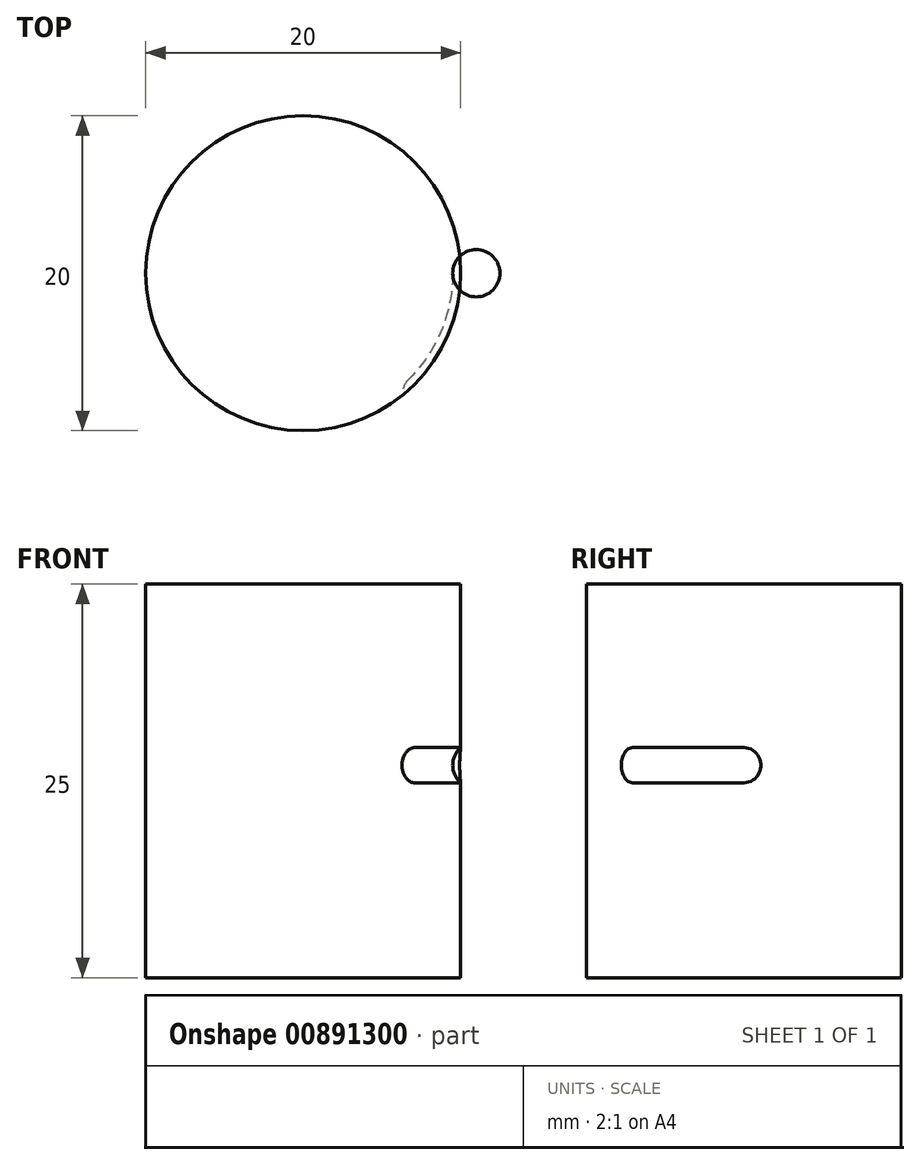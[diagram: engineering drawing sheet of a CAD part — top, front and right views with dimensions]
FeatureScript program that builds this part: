
annotation { "Feature Type Name" : "Feature", "Feature Type Description" : "" }
export const myFeature = defineFeature(function(context is Context, id is Id, definition is map)
    precondition{}
    {
        {
            var Q0;
            Q0=qCreatedBy(makeId("Top.planeOp"),FACE);
            var sketch = newSketch(context, id + "F0", { "sketchPlane" : qUnion([Q0])});
            skCircle(sketch, "E0", {"center": v(0, 0) * mm, "radius": 10 * mm});
            skSolve(sketch);
        }
        {
            var Q0;
            Q0 = qSketchRegion(id + "F0", true);
            extrude(context, id + "F1", {"entities" : qUnion([Q0]), "depth" : 25 * mm, "offsetDistance" : 25 * mm});
        }
        {
            var Q0;
            Q0=qCreatedBy(makeId("Front.planeOp"),FACE);
            var sketch = newSketch(context, id + "F2", { "sketchPlane" : qUnion([Q0])});
            skArc(sketch, "E1", {"start": v(11, 15) * mm, "mid": v(9.5, 13.5) * mm, "end": v(11, 12) * mm});
            skLineSegment(sketch, "E2", {"start": v(10, 25) * mm, "end": v(10, 0) * mm, "construction": true});
            skLineSegment(sketch, "E3", {"start": v(11, 15) * mm, "end": v(11, 12) * mm});
            skSolve(sketch);
        }
        {
            var Q0;
            Q0 = qSketchRegion(id + "F2", true);
            var Q1;
            Q1=makeQuery(id+"F1.opExtrude","CAP_EDGE",EDGE,{"disambiguationData":[OSD([sQuery(id+"F0.wireOp",EDGE,"E0")])],"isStart":false});
            revolve(context, id + "F3", {"operationType" : NewBodyOperationType.REMOVE, "surfaceOperationType" : NewSurfaceOperationType.NEW, "entities" : qUnion([Q0]), "axis" : qUnion([Q1]), "revolveType" : RevolveType.ONE_DIRECTION, "oppositeDirection" : true, "angle" : 45 * degree});
        }
        {
            var Q0;
            Q0=makeQuery(id+"F2.imprint","IMPRINT",FACE,{"disambiguationData":[TD([[makeQuery(id+"F2.imprint","IMPRINT",EDGE,{"derivedFrom":sQuery(id+"F2.wireOp",EDGE,"E1")}),1.0]])]});
            var Q1;
            Q1=sQuery(id+"F2.wireOp",EDGE,"E3");
            revolve(context, id + "F4", {"surfaceOperationType" : NewSurfaceOperationType.NEW, "entities" : qUnion([Q0]), "axis" : qUnion([Q1]), "revolveType" : RevolveType.FULL});
        }
        {
            var Q0;
            Q0=makeQuery(id+"F4.opRevolve","SWEPT_BODY",BODY,{"disambiguationData":[OSD([sQuery(id+"F2.wireOp",EDGE,"E1"),sQuery(id+"F2.wireOp",EDGE,"E3")])]});
            var Q1;
            Q1=makeQuery(id+"F1.opExtrude","CAP_EDGE",EDGE,{"disambiguationData":[OSD([sQuery(id+"F0.wireOp",EDGE,"E0")])],"isStart":false});
            transform(context, id + "F5", {"entities" : qUnion([Q0]), "transformType" : TransformType.ROTATION, "transformAxis" : qUnion([Q1]), "angle" : 45 * degree, "oppositeDirection" : true, "makeCopy" : true});
        }
        {
            var Q0;
            Q0=makeQuery(id+"F5.opPattern","COPY",BODY,{"derivedFrom":makeQuery(id+"F4.opRevolve","SWEPT_BODY",BODY,{"disambiguationData":[OSD([sQuery(id+"F2.wireOp",EDGE,"E1"),sQuery(id+"F2.wireOp",EDGE,"E3")])]}),"instanceName":"1"});
            var Q1;
            Q1=makeQuery(id+"F4.opRevolve","SWEPT_BODY",BODY,{"disambiguationData":[OSD([sQuery(id+"F2.wireOp",EDGE,"E1"),sQuery(id+"F2.wireOp",EDGE,"E3")])]});
            var Q2;
            Q2=makeQuery(id+"F1.opExtrude","SWEPT_BODY",BODY,{"disambiguationData":[OSD([sQuery(id+"F0.wireOp",EDGE,"E0")])]});
            booleanBodies(context, id + "F6", {"operationType" : BooleanOperationType.SUBTRACTION, "tools" : qUnion([Q0, Q1]), "targets" : qUnion([Q2])});
        }
    });
